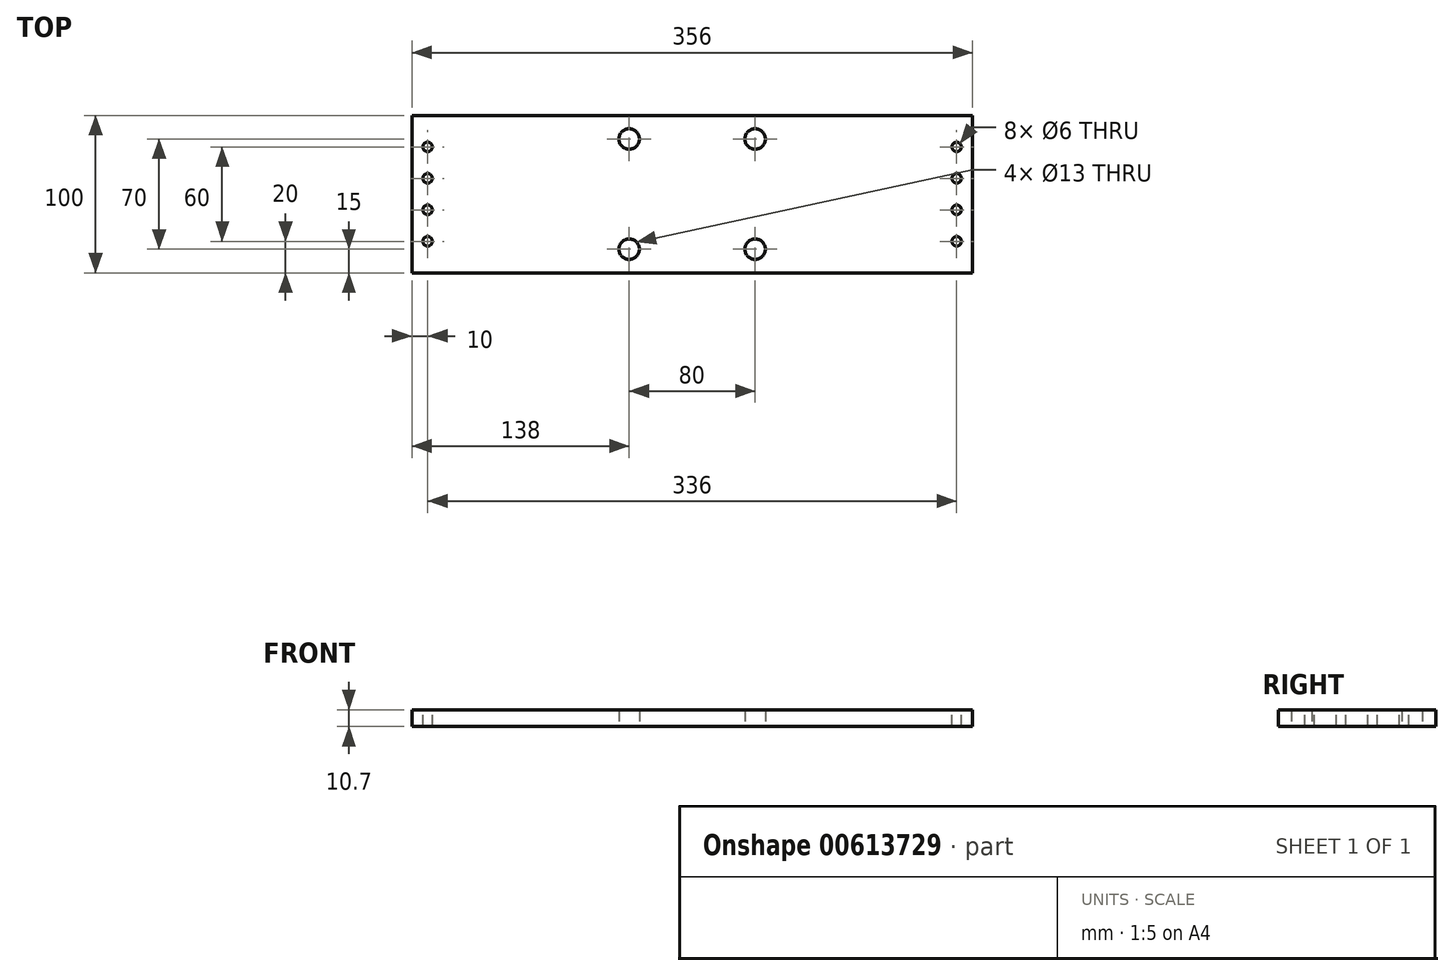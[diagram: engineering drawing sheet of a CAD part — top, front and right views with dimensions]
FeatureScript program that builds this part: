
annotation { "Feature Type Name" : "Feature", "Feature Type Description" : "" }
export const myFeature = defineFeature(function(context is Context, id is Id, definition is map)
    precondition{}
    {
        {
            var Q0;
            Q0=qCreatedBy(makeId("Top.planeOp"),FACE);
            var sketch = newSketch(context, id + "F0", { "sketchPlane" : qUnion([Q0])});
            skLineSegment(sketch, "E0.bottom", {"start": v(178, 50) * mm, "end": v(-178, 50) * mm});
            skLineSegment(sketch, "E0.top", {"start": v(178, -50) * mm, "end": v(-178, -50) * mm});
            skLineSegment(sketch, "E0.left", {"start": v(178, 50) * mm, "end": v(178, -50) * mm});
            skLineSegment(sketch, "E0.right", {"start": v(-178, 50) * mm, "end": v(-178, -50) * mm});
            skPoint(sketch, "E0.middle", {"position": v(0, 0) * mm});
            skCircle(sketch, "E1", {"center": v(-40, 35) * mm, "radius": 6.5 * mm});
            skCircle(sketch, "E2", {"center": v(40, 35) * mm, "radius": 6.5 * mm});
            skCircle(sketch, "E3", {"center": v(-40, -35) * mm, "radius": 6.5 * mm});
            skCircle(sketch, "E4", {"center": v(40, -35) * mm, "radius": 6.5 * mm});
            skLineSegment(sketch, "E5", {"start": v(-40, 35) * mm, "end": v(40, 35) * mm, "construction": true});
            skLineSegment(sketch, "E6", {"start": v(40, -35) * mm, "end": v(40, 35) * mm, "construction": true});
            skPoint(sketch, "E7", {"position": v(0, 35) * mm});
            skPoint(sketch, "E8", {"position": v(40, 0) * mm});
            skSolve(sketch);
        }
        {
            var Q0;
            Q0=qSketchRegion(id+"F0",true);
            extrude(context, id + "F1", {"entities" : qUnion([Q0]), "depth" : 10.7 * mm, "offsetDistance" : 25 * mm});
        }
        {
            var Q0;
            Q0=makeQuery(id+"F1.opExtrude","CAP_FACE",FACE,{"disambiguationData":[OSD([sQuery(id+"F0.wireOp",EDGE,"E0.bottom"),sQuery(id+"F0.wireOp",EDGE,"E0.top"),sQuery(id+"F0.wireOp",EDGE,"E0.left"),sQuery(id+"F0.wireOp",EDGE,"E0.right"),sQuery(id+"F0.wireOp",EDGE,"E1"),sQuery(id+"F0.wireOp",EDGE,"E2"),sQuery(id+"F0.wireOp",EDGE,"E3"),sQuery(id+"F0.wireOp",EDGE,"E4")])],"isStart":false});
            var sketch = newSketch(context, id + "F2", { "sketchPlane" : qUnion([Q0])});
            skCircle(sketch, "E9", {"center": v(168, -30) * mm, "radius": 3 * mm});
            skCircle(sketch, "E10", {"center": v(168, -10) * mm, "radius": 3 * mm});
            skCircle(sketch, "E11", {"center": v(168, 10) * mm, "radius": 3 * mm});
            skCircle(sketch, "E12", {"center": v(168, 30) * mm, "radius": 3 * mm});
            skLineSegment(sketch, "E13", {"start": v(168, -30) * mm, "end": v(168, -10) * mm, "construction": true});
            skLineSegment(sketch, "E14", {"start": v(168, 10) * mm, "end": v(168, 30) * mm, "construction": true});
            skLineSegment(sketch, "E15", {"start": v(168, 10) * mm, "end": v(168, -10) * mm, "construction": true});
            skPoint(sketch, "E16", {"position": v(168, 0) * mm});
            skLineSegment(sketch, "E17", {"start": v(168, 30) * mm, "end": v(168, 50) * mm, "construction": true});
            skLineSegment(sketch, "E18", {"start": v(0, -50) * mm, "end": v(0, 50) * mm, "construction": true});
            skCircle(sketch, "E19.MirrorC", {"center": v(-168, -30) * mm, "radius": 3 * mm});
            skPoint(sketch, "E20.MirrorP", {"position": v(-168, 0) * mm});
            skLineSegment(sketch, "E21.MirrorCS", {"start": v(-168, 30) * mm, "end": v(-168, 50) * mm, "construction": true});
            skCircle(sketch, "E22.MirrorC", {"center": v(-168, 10) * mm, "radius": 3 * mm});
            skLineSegment(sketch, "E23.MirrorCS", {"start": v(-168, 10) * mm, "end": v(-168, -10) * mm, "construction": true});
            skLineSegment(sketch, "E24.MirrorCS", {"start": v(-168, -30) * mm, "end": v(-168, -10) * mm, "construction": true});
            skLineSegment(sketch, "E25.MirrorCS", {"start": v(-168, 10) * mm, "end": v(-168, 30) * mm, "construction": true});
            skCircle(sketch, "E26.MirrorC", {"center": v(-168, 30) * mm, "radius": 3 * mm});
            skCircle(sketch, "E27.MirrorC", {"center": v(-168, -10) * mm, "radius": 3 * mm});
            skSolve(sketch);
        }
        {
            var Q0;
            Q0=qSketchRegion(id+"F2",true);
            extrude(context, id + "F3", {"entities" : qUnion([Q0]), "operationType" : NewBodyOperationType.REMOVE, "oppositeDirection" : true, "depth" : 25 * mm, "offsetDistance" : 25 * mm});
        }
    });
